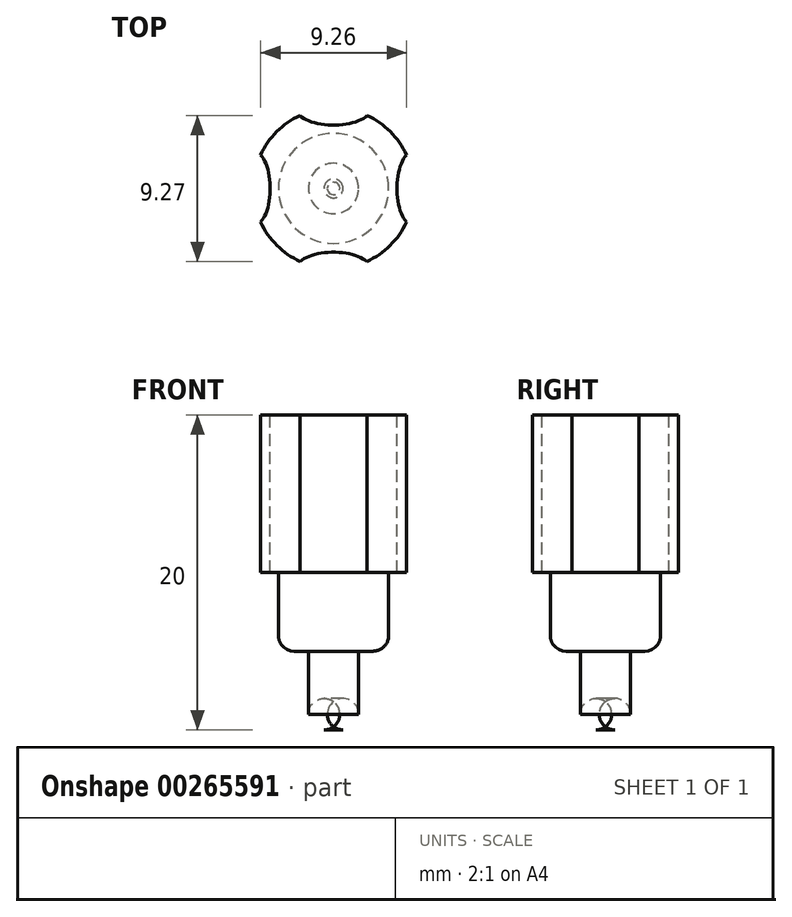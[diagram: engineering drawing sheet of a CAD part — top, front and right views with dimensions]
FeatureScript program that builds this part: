
annotation { "Feature Type Name" : "Feature", "Feature Type Description" : "" }
export const myFeature = defineFeature(function(context is Context, id is Id, definition is map)
    precondition{}
    {
        {
            var Q0;
            Q0=qCreatedBy(makeId("Top.planeOp"),FACE);
            var sketch = newSketch(context, id + "F0", { "sketchPlane" : qUnion([Q0])});
            skCircle(sketch, "E0", {"center": v(0, 0) * mm, "radius": 3.5 * mm});
            skCircle(sketch, "E1", {"center": v(0, 0) * mm, "radius": 1.6 * mm});
            skCircle(sketch, "E2", {"center": v(0, 0) * mm, "radius": 5.1 * mm});
            skEllipse(sketch, "E3", {"center": v(-5.1, 0) * mm, "majorRadius": 1.08 * mm, "minorRadius": 2.36 * mm, "majorAxis": v(1, 0)});
            skEllipse(sketch, "E4", {"center": v(5.1, 0) * mm, "majorRadius": 1.08 * mm, "minorRadius": 2.36 * mm, "majorAxis": v(1, 0)});
            skEllipse(sketch, "E5", {"center": v(0, 5.1) * mm, "majorRadius": 1.08 * mm, "minorRadius": 2.36 * mm, "majorAxis": v(0, -1)});
            skEllipse(sketch, "E6", {"center": v(0, -5.12) * mm, "majorRadius": 1.08 * mm, "minorRadius": 2.36 * mm, "majorAxis": v(0, -1)});
            skSolve(sketch);
        }
        {
            var Q0;
            Q0=makeQuery(id+"F0.imprint","IMPRINT",FACE,{"disambiguationData":[TD([[makeQuery(id+"F0.imprint","IMPRINT",EDGE,{"derivedFrom":sQuery(id+"F0.wireOp",EDGE,"E0")}),-1.0]])]});
            var Q1;
            Q1=makeQuery(id+"F0.imprint","IMPRINT",FACE,{"disambiguationData":[TD([[makeQuery(id+"F0.imprint","IMPRINT",EDGE,{"derivedFrom":sQuery(id+"F0.wireOp",EDGE,"E0")}),1.0]])]});
            var Q2;
            Q2=makeQuery(id+"F0.imprint","IMPRINT",FACE,{"disambiguationData":[TD([[makeQuery(id+"F0.imprint","IMPRINT",EDGE,{"derivedFrom":sQuery(id+"F0.wireOp",EDGE,"E1")}),1.0]])]});
            extrude(context, id + "F1", {"entities" : qUnion([Q0, Q1, Q2]), "oppositeDirection" : true, "depth" : 10 * mm});
        }
        {
            var Q0;
            Q0=makeQuery(id+"F0.imprint","IMPRINT",FACE,{"disambiguationData":[TD([[makeQuery(id+"F0.imprint","IMPRINT",EDGE,{"derivedFrom":sQuery(id+"F0.wireOp",EDGE,"E0")}),1.0]])]});
            extrude(context, id + "F2", {"entities" : qUnion([Q0]), "operationType" : NewBodyOperationType.ADD, "oppositeDirection" : true, "depth" : (10 + 5) * mm});
        }
        {
            var Q0;
            Q0=makeQuery(id+"F0.imprint","IMPRINT",FACE,{"disambiguationData":[TD([[makeQuery(id+"F0.imprint","IMPRINT",EDGE,{"derivedFrom":sQuery(id+"F0.wireOp",EDGE,"E1")}),1.0]])]});
            extrude(context, id + "F3", {"entities" : qUnion([Q0]), "operationType" : NewBodyOperationType.ADD, "oppositeDirection" : true, "depth" : (10 + 10) * mm});
        }
        {
            var Q0;
            Q0=makeQuery(id+"F3.opExtrude","CAP_EDGE",EDGE,{"disambiguationData":[OSD([sQuery(id+"F0.wireOp",EDGE,"E1")])],"isStart":false});
            fillet(context, id + "F4", {"entities" : qUnion([Q0]), "radius" : 1 * mm, "tangentPropagation" : true, "allowEdgeOverflow" : false});
        }
        {
            var Q0;
            Q0=makeQuery(id+"F2.opExtrude","CAP_EDGE",EDGE,{"disambiguationData":[OSD([sQuery(id+"F0.wireOp",EDGE,"E0")])],"isStart":false});
            fillet(context, id + "F5", {"entities" : qUnion([Q0]), "radius" : 1 * mm, "tangentPropagation" : true, "allowEdgeOverflow" : false});
        }
    });
